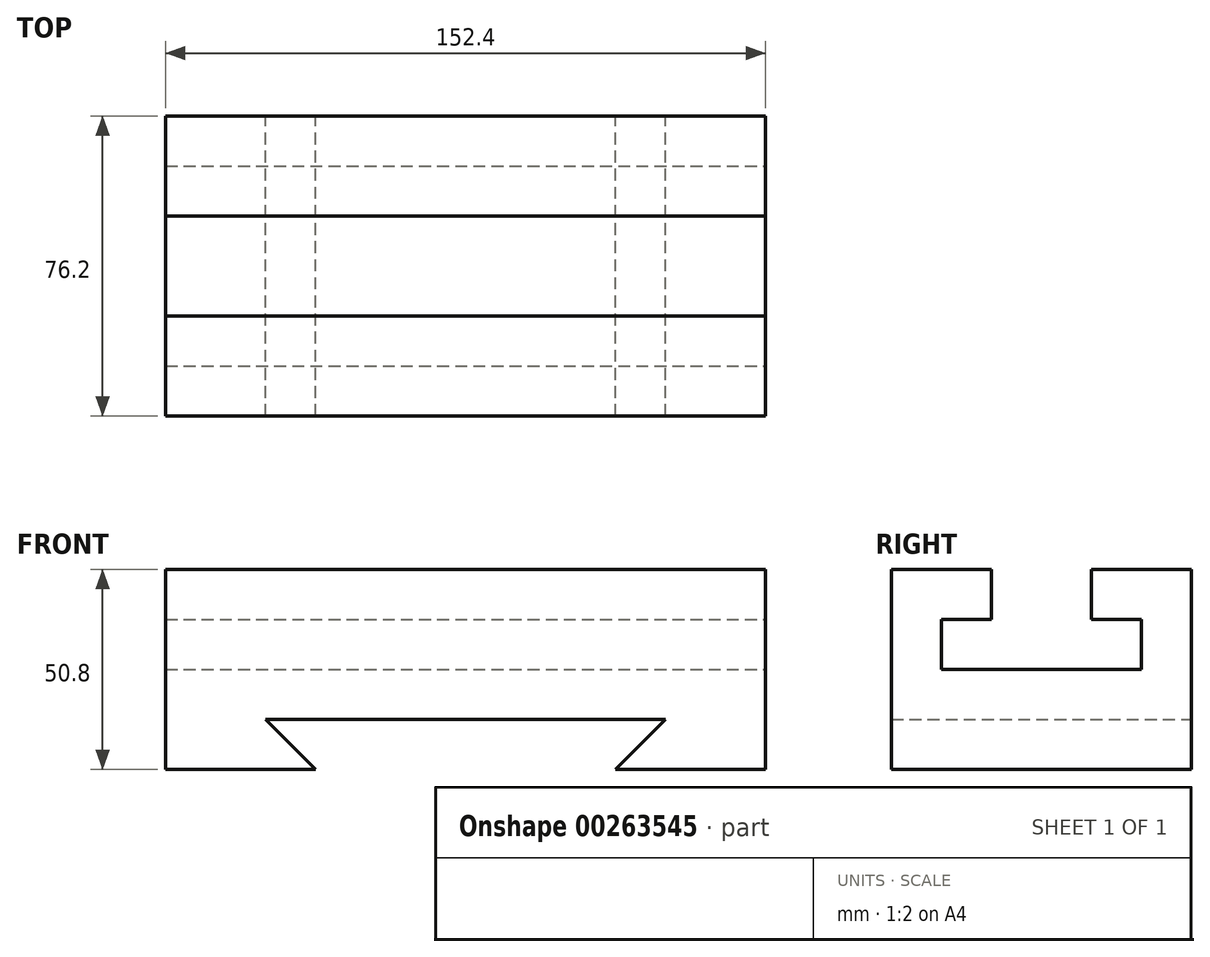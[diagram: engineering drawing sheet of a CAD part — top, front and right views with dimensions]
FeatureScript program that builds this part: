
annotation { "Feature Type Name" : "Feature", "Feature Type Description" : "" }
export const myFeature = defineFeature(function(context is Context, id is Id, definition is map)
    precondition{}
    {
        {
            var Q0;
            Q0=qCreatedBy(makeId("Front.planeOp"),FACE);
            var sketch = newSketch(context, id + "F0", { "sketchPlane" : qUnion([Q0])});
            skLineSegment(sketch, "E0", {"start": v(-65.33, -31.37) * mm, "end": v(-27.23, -31.37) * mm});
            skLineSegment(sketch, "E1", {"start": v(-65.33, -31.37) * mm, "end": v(-65.33, 19.43) * mm});
            skLineSegment(sketch, "E2", {"start": v(-65.33, 19.43) * mm, "end": v(87.07, 19.43) * mm});
            skLineSegment(sketch, "E3", {"start": v(87.07, 19.43) * mm, "end": v(87.07, -31.37) * mm});
            skLineSegment(sketch, "E4", {"start": v(87.07, -31.37) * mm, "end": v(48.97, -31.37) * mm});
            skLineSegment(sketch, "E5.trimOffspring", {"start": v(48.97, -31.37) * mm, "end": v(87.07, -31.37) * mm});
            skLineSegment(sketch, "E6", {"start": v(-65.33, -31.37) * mm, "end": v(-65.33, -18.67) * mm});
            skLineSegment(sketch, "E7", {"start": v(-27.23, -31.37) * mm, "end": v(-39.93, -18.67) * mm});
            skLineSegment(sketch, "E8", {"start": v(-39.93, -18.67) * mm, "end": v(61.67, -18.67) * mm});
            skLineSegment(sketch, "E9", {"start": v(48.97, -31.37) * mm, "end": v(61.67, -18.67) * mm});
            skSolve(sketch);
        }
        {
            var Q0;
            Q0=makeQuery(id+"F0.imprint","IMPRINT",FACE,{"disambiguationData":[TD([[makeQuery(id+"F0.imprint","IMPRINT",EDGE,{"derivedFrom":sQuery(id+"F0.wireOp",EDGE,"E1")}),-1.0]])]});
            extrude(context, id + "F1", {"entities" : qUnion([Q0]), "depth" : 76.2 * mm});
        }
        {
            var Q0;
            Q0=makeQuery(id+"F1.opExtrude","SWEPT_FACE",FACE,{"disambiguationData":[OSD([sQuery(id+"F0.wireOp",EDGE,"E3")])]});
            var sketch = newSketch(context, id + "F2", { "sketchPlane" : qUnion([Q0])});
            skLineSegment(sketch, "E10", {"start": v(-76.2, 19.43) * mm, "end": v(-50.8, 19.43) * mm});
            skLineSegment(sketch, "E11", {"start": v(-50.8, 19.43) * mm, "end": v(-50.8, 6.73) * mm});
            skLineSegment(sketch, "E12", {"start": v(-50.8, 6.73) * mm, "end": v(-63.5, 6.73) * mm});
            skLineSegment(sketch, "E13", {"start": v(-63.5, 6.73) * mm, "end": v(-63.5, -5.97) * mm});
            skLineSegment(sketch, "E14", {"start": v(-63.5, -5.97) * mm, "end": v(-12.7, -5.97) * mm});
            skLineSegment(sketch, "E15", {"start": v(-12.7, -5.97) * mm, "end": v(-12.7, 6.73) * mm});
            skLineSegment(sketch, "E16", {"start": v(-12.7, 6.73) * mm, "end": v(-25.4, 6.73) * mm});
            skLineSegment(sketch, "E17", {"start": v(-25.4, 6.73) * mm, "end": v(-25.4, 19.43) * mm});
            skSolve(sketch);
        }
        {
            var Q0;
            {var subQ0=sQuery(id+"F2.wireOp",EDGE,"E11");Q0=makeQuery(id+"F2.imprint","IMPRINT",FACE,{"disambiguationData":[TD([[makeQuery(id+"F2.imprint","IMPRINT",EDGE,{"derivedFrom":subQ0}),1.0]])]});}
            extrude(context, id + "F3", {"entities" : qUnion([Q0]), "operationType" : NewBodyOperationType.REMOVE, "oppositeDirection" : true, "depth" : 152.4 * mm});
        }
    });
